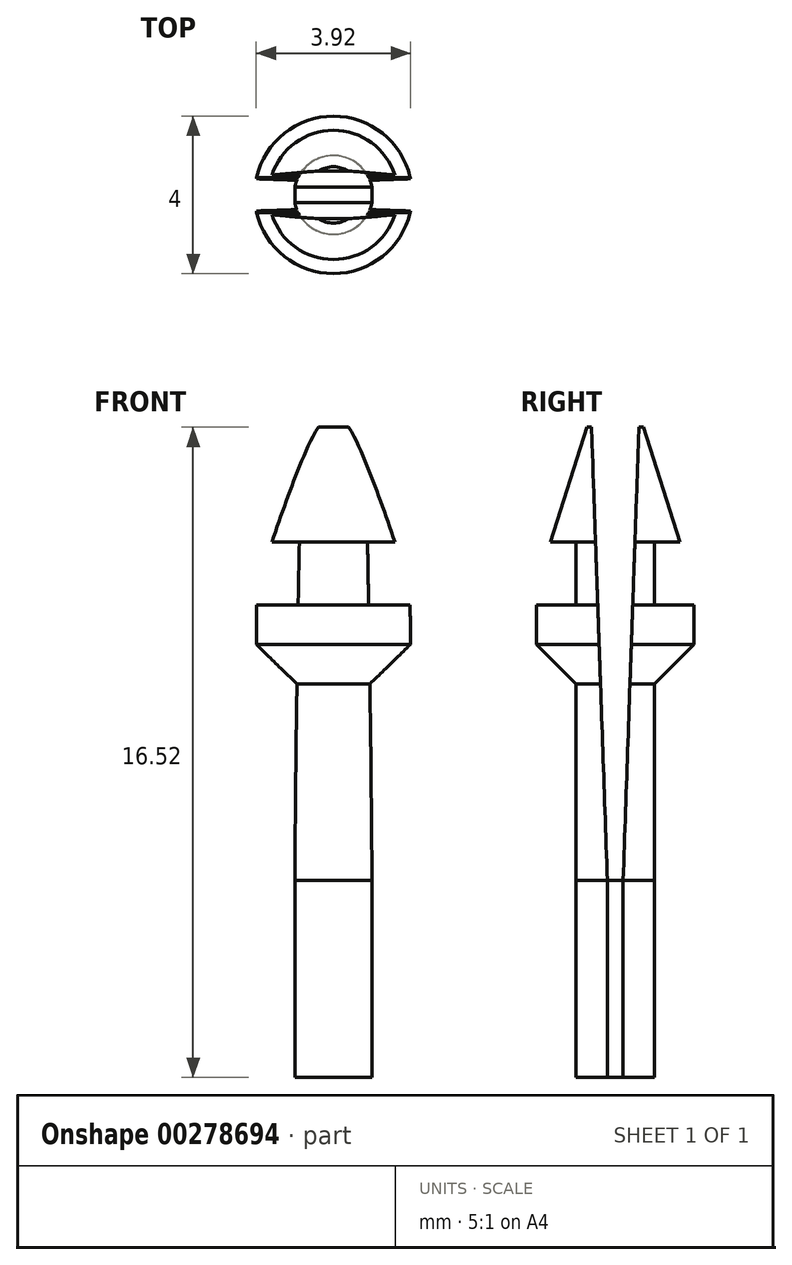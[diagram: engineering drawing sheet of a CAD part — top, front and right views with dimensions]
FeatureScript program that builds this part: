
annotation { "Feature Type Name" : "Feature", "Feature Type Description" : "" }
export const myFeature = defineFeature(function(context is Context, id is Id, definition is map)
    precondition{}
    {
        {
            var Q0;
            Q0=qCreatedBy(makeId("Front.planeOp"),FACE);
            var sketch = newSketch(context, id + "F0", { "sketchPlane" : qUnion([Q0])});
            skLineSegment(sketch, "E0", {"start": v(0, 0) * mm, "end": v(-1, 0) * mm});
            skLineSegment(sketch, "E1", {"start": v(0, 1.5) * mm, "end": v(-0.3, 1.5) * mm});
            skLineSegment(sketch, "E2", {"start": v(-1, 0) * mm, "end": v(-1, 5) * mm});
            skLineSegment(sketch, "E3", {"start": v(-2, 6) * mm, "end": v(-2, 7) * mm});
            skLineSegment(sketch, "E4", {"start": v(-2, 7) * mm, "end": v(-1, 7) * mm});
            skLineSegment(sketch, "E5", {"start": v(-1, 7) * mm, "end": v(-1, 8.6) * mm});
            skLineSegment(sketch, "E6", {"start": v(-1, 8.6) * mm, "end": v(-1.64, 8.6) * mm});
            skLineSegment(sketch, "E7", {"start": v(-1.64, 8.6) * mm, "end": v(-0.71, 11.52) * mm});
            skLineSegment(sketch, "E8", {"start": v(-0.71, 11.52) * mm, "end": v(0, 11.52) * mm});
            skLineSegment(sketch, "E9", {"start": v(0, 11.52) * mm, "end": v(0, 0) * mm});
            skLineSegment(sketch, "E10", {"start": v(-1, 5) * mm, "end": v(-2, 6) * mm});
            skPoint(sketch, "E11.end.orphan", {"position": v(-2, 5) * mm});
            skSolve(sketch);
        }
        {
            var Q0;
            Q0=qSketchRegion(id+"F0",true);
            var Q1;
            Q1=sQuery(id+"F0.wireOp",EDGE,"E9");
            revolve(context, id + "F1", {"entities" : qUnion([Q0]), "axis" : qUnion([Q1]), "revolveType" : RevolveType.FULL});
        }
        {
            var Q0;
            Q0=qCreatedBy(makeId("Right.planeOp"),FACE);
            var sketch = newSketch(context, id + "F2", { "sketchPlane" : qUnion([Q0])});
            skLineSegment(sketch, "E12", {"start": v(-0.33, 7) * mm, "end": v(0.33, 7) * mm});
            skPoint(sketch, "E13.middle", {"position": v(0, 0) * mm});
            skLineSegment(sketch, "E14", {"start": v(0, 0) * mm, "end": v(-0.2, 0) * mm});
            skLineSegment(sketch, "E15", {"start": v(0, 0) * mm, "end": v(0.2, 0) * mm});
            skLineSegment(sketch, "E16", {"start": v(-0.2, 0) * mm, "end": v(-0.64, 12.53) * mm});
            skLineSegment(sketch, "E17", {"start": v(0.2, 0) * mm, "end": v(0.64, 12.6) * mm});
            skLineSegment(sketch, "E18", {"start": v(-0.64, 12.53) * mm, "end": v(0.64, 12.6) * mm});
            skSolve(sketch);
        }
        {
            var Q0;
            Q0=makeQuery(id+"F2.imprint","IMPRINT",FACE,{"disambiguationData":[TD([[makeQuery(id+"F2.imprint","IMPRINT",EDGE,{"derivedFrom":sQuery(id+"F2.wireOp",EDGE,"E14")}),-1.0]])]});
            extrude(context, id + "F3", {"entities" : qUnion([Q0]), "operationType" : NewBodyOperationType.REMOVE, "endBound" : BoundingType.SYMMETRIC, "oppositeDirection" : true, "depth" : 200 * mm});
        }
        {
            var Q0;
            Q0=makeQuery(id+"F3.boolean.opBoolean","SPLIT",FACE,{"disambiguationData":[TD([makeQuery(id+"F3.opExtrude","SWEPT_FACE",FACE,{"disambiguationData":[OSD([sQuery(id+"F2.wireOp",EDGE,"E16")])]})])],"derivedFrom":makeQuery(id+"F1.opRevolve","SWEPT_FACE",FACE,{"disambiguationData":[OSD([sQuery(id+"F0.wireOp",EDGE,"E0")])]})});
            var sketch = newSketch(context, id + "F4", { "sketchPlane" : qUnion([Q0])});
            skLineSegment(sketch, "E19.bottom", {"start": v(0.98, 0.2) * mm, "end": v(-0.98, 0.2) * mm});
            skLineSegment(sketch, "E19.top", {"start": v(0.98, -0.2) * mm, "end": v(-0.98, -0.2) * mm});
            skLineSegment(sketch, "E19.left", {"start": v(0.98, 0.2) * mm, "end": v(0.98, -0.2) * mm});
            skLineSegment(sketch, "E19.right", {"start": v(-0.98, 0.2) * mm, "end": v(-0.98, -0.2) * mm});
            skSolve(sketch);
        }
        {
            var Q0;
            Q0=makeQuery(id+"F4.imprint","IMPRINT",FACE,{"disambiguationData":[TD([[makeQuery(id+"F4.imprint","IMPRINT",EDGE,{"derivedFrom":sQuery(id+"F4.wireOp",EDGE,"E19.bottom")}),1.0]])]});
            var Q1;
            Q1=makeQuery(id+"F3.boolean.opBoolean","SPLIT",FACE,{"disambiguationData":[TD([makeQuery(id+"F3.opExtrude","SWEPT_FACE",FACE,{"disambiguationData":[OSD([sQuery(id+"F2.wireOp",EDGE,"E17")])]})])],"derivedFrom":makeQuery(id+"F1.opRevolve","SWEPT_FACE",FACE,{"disambiguationData":[OSD([sQuery(id+"F0.wireOp",EDGE,"E0")])]})});
            var Q2;
            Q2=makeQuery(id+"F4.imprint","IMPRINT",FACE,{"disambiguationData":[TD([[makeQuery(id+"F4.imprint","IMPRINT",EDGE,{"derivedFrom":sQuery(id+"F4.wireOp",EDGE,"E19.bottom")}),-1.0]])]});
            extrude(context, id + "F5", {"entities" : qUnion([Q0, Q1, Q2]), "depth" : 5 * mm});
        }
        {
            var Q0;
            Q0=makeQuery(id+"F5.opExtrude","SWEPT_BODY",BODY,{"disambiguationData":[OSD([sQuery(id+"F0.wireOp",EDGE,"E0"),sQuery(id+"F0.wireOp",EDGE,"E2"),sQuery(id+"F4.wireOp",EDGE,"E19.top"),sQuery(id+"F4.wireOp",EDGE,"E19.left"),sQuery(id+"F4.wireOp",EDGE,"E19.right")])]});
            var Q1;
            Q1=makeQuery(id+"F5.opExtrude","SWEPT_BODY",BODY,{"disambiguationData":[OSD([sQuery(id+"F0.wireOp",EDGE,"E0")])]});
            booleanBodies(context, id + "F6", {"operationType" : BooleanOperationType.UNION, "tools" : qUnion([Q0, Q1])});
        }
    });
